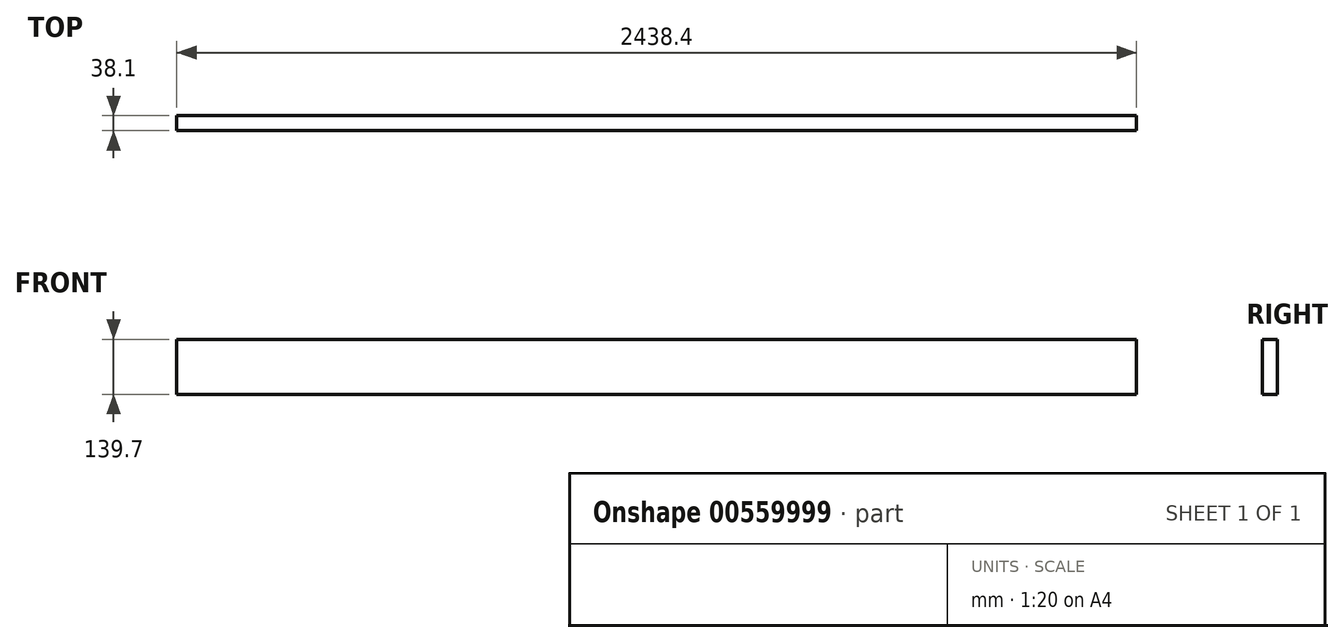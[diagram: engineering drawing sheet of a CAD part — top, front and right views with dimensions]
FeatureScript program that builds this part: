
annotation { "Feature Type Name" : "Feature", "Feature Type Description" : "" }
export const myFeature = defineFeature(function(context is Context, id is Id, definition is map)
    precondition{}
    {
        {
            var Q0;
            Q0=qCreatedBy(makeId("Right.planeOp"),FACE);
            var sketch = newSketch(context, id + "F0", { "sketchPlane" : qUnion([Q0])});
            skLineSegment(sketch, "E0.bottom", {"start": v(19.05, -69.85) * mm, "end": v(-19.05, -69.85) * mm});
            skLineSegment(sketch, "E0.top", {"start": v(19.05, 69.85) * mm, "end": v(-19.05, 69.85) * mm});
            skLineSegment(sketch, "E0.left", {"start": v(19.05, -69.85) * mm, "end": v(19.05, 69.85) * mm});
            skLineSegment(sketch, "E0.right", {"start": v(-19.05, -69.85) * mm, "end": v(-19.05, 69.85) * mm});
            skPoint(sketch, "E0.middle", {"position": v(0, 0) * mm});
            skSolve(sketch);
        }
        {
            var Q0;
            Q0=qSketchRegion(id+"F0",true);
            extrude(context, id + "F1", {"entities" : qUnion([Q0]), "endBound" : BoundingType.SYMMETRIC, "depth" : 2438.4 * mm, "offsetDistance" : 25.4 * mm});
        }
    });
